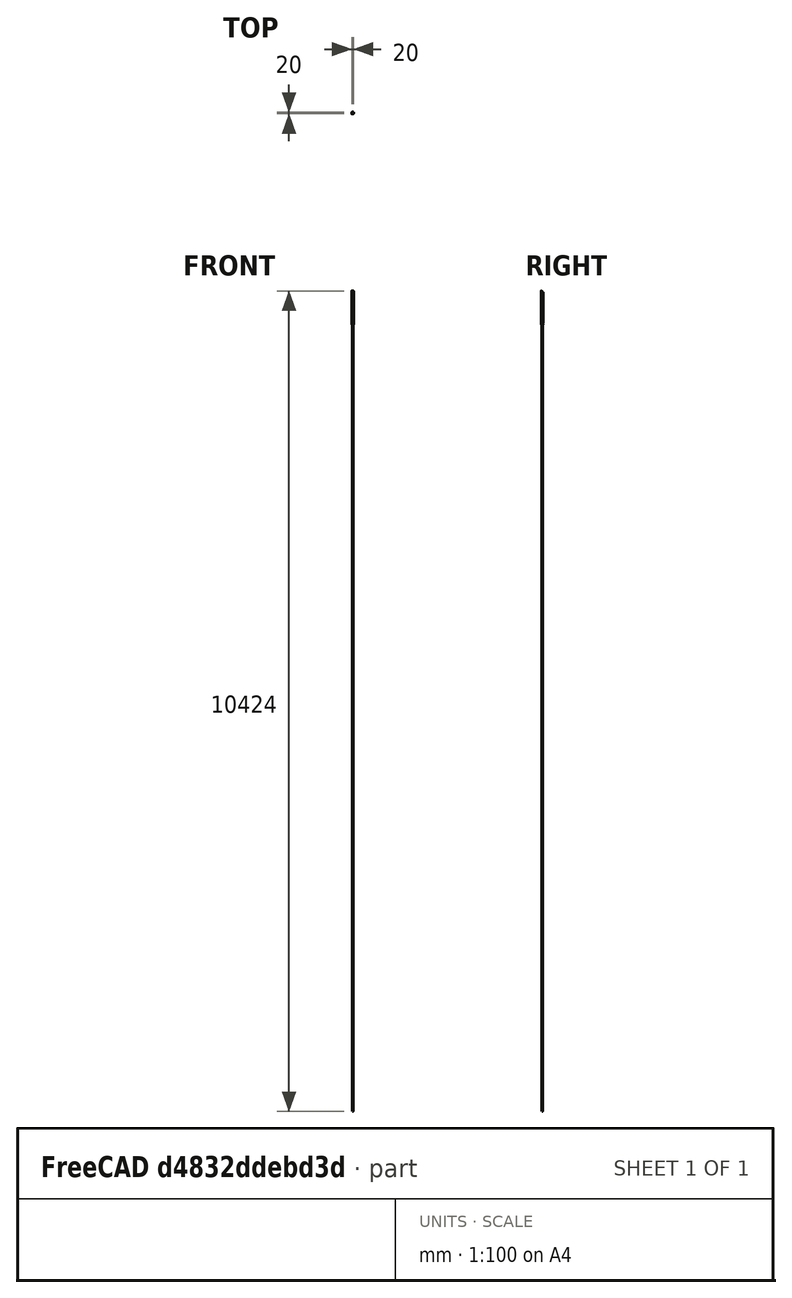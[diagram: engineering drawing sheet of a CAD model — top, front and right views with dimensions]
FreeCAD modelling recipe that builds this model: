
FCSTD DOCUMENT  (FreeCAD 0.15R4671 (Git))
Label: prueba perfil 425mm 1
License: CC-BY 3.0
LicenseURL: http://creativecommons.org/licenses/by/3.0/
objects: Sketcher::SketchObject×2, Part::Extrusion×2, Part::Cut×2, Part::Box×2, PartDesign::Pad×1, PartDesign::Pocket×1, Part::MultiFuse×1
note: 13 computed .brp shape members not serialized (recipe doc carries the construction recipe); baked Part::Feature solids carry a one-line shape summary decoded from their .brp

FEATURE [Sketcher::SketchObject] Sketch
  Placement = pos=(1.5,0,0) rot=(0,0,1;0rad)
  sketch-geometry (136):
    g0: LineSegment StartX=0 StartY=20 StartZ=0 EndX=4.65 EndY=20 EndZ=0
    g1: ArcOfCircle CenterX=-1e-12 CenterY=18.5 CenterZ=0 NormalX=0 NormalY=0 NormalZ=1 Radius=1.5 StartAngle=1.5708 EndAngle=3.14159
    g2: LineSegment StartX=-1.5 StartY=13.85 StartZ=0 EndX=-1.5 EndY=18.5 EndZ=0
    g3: ArcOfCircle CenterX=-1.3 CenterY=13.85 CenterZ=0 NormalX=0 NormalY=0 NormalZ=1 Radius=0.2 StartAngle=3.14159 EndAngle=4.71239
    g4: LineSegment StartX=-1 StartY=13.65 StartZ=0 EndX=-1.3 EndY=13.65 EndZ=0
    g5: LineSegment StartX=-1 StartY=13.3 StartZ=0 EndX=-1 EndY=13.65 EndZ=0
    g6: ArcOfCircle CenterX=-0.8 CenterY=13.3 CenterZ=0 NormalX=0 NormalY=0 NormalZ=1 Radius=0.2 StartAngle=3.14159 EndAngle=4.71239
    g7: LineSegment StartX=-0.5 StartY=13.1 StartZ=0 EndX=-0.8 EndY=13.1 EndZ=0
    g8: ArcOfCircle CenterX=-0.5 CenterY=13.6 CenterZ=0 NormalX=0 NormalY=0 NormalZ=1 Radius=0.5 StartAngle=4.71239 EndAngle=6.28319
    g9: LineSegment StartX=2.68e-07 StartY=15.5 StartZ=0 EndX=2.68e-07 EndY=13.6 EndZ=0
    g10: ArcOfCircle CenterX=0.5 CenterY=15.5 CenterZ=0 NormalX=0 NormalY=0 NormalZ=1 Radius=0.5 StartAngle=1.5708 EndAngle=3.14159
    g11: LineSegment StartX=1.23223 StartY=16 StartZ=0 EndX=0.5 EndY=16 EndZ=0
    g12: ArcOfCircle CenterX=1.23223 CenterY=15.5 CenterZ=0 NormalX=0 NormalY=0 NormalZ=1 Radius=0.5 StartAngle=0.785398 EndAngle=1.5708
    g13: LineSegment StartX=3.85355 StartY=13.5858 StartZ=0 EndX=1.58579 EndY=15.8536 EndZ=0
    g14: ArcOfCircle CenterX=3.5 CenterY=13.2322 CenterZ=0 NormalX=0 NormalY=0 NormalZ=1 Radius=0.5 StartAngle=0 EndAngle=0.785398
    g15: LineSegment StartX=4 StartY=10.9536 StartZ=0 EndX=4 EndY=13.2322 EndZ=0
    g16: ArcOfCircle CenterX=4.2 CenterY=10.9536 CenterZ=0 NormalX=0 NormalY=0 NormalZ=1 Radius=0.2 StartAngle=3.14159 EndAngle=3.66519
    g17: LineSegment StartX=4.46188 StartY=10.1 StartZ=0 EndX=4.0268 EndY=10.8536 EndZ=0
    g18: ArcOfCircle CenterX=4.28868 CenterY=10 CenterZ=0 NormalX=0 NormalY=0 NormalZ=1 Radius=0.2 StartAngle=5.75959 EndAngle=6.80678
    g19: LineSegment StartX=4.0268 StartY=9.14641 StartZ=0 EndX=4.46188 EndY=9.9 EndZ=0
    g20: ArcOfCircle CenterX=4.2 CenterY=9.04641 CenterZ=0 NormalX=0 NormalY=0 NormalZ=1 Radius=0.2 StartAngle=2.61799 EndAngle=3.14159
    g21: LineSegment StartX=4 StartY=6.76777 StartZ=0 EndX=4 EndY=9.04641 EndZ=0
    g22: ArcOfCircle CenterX=3.5 CenterY=6.76777 CenterZ=0 NormalX=0 NormalY=0 NormalZ=1 Radius=0.5 StartAngle=5.49779 EndAngle=6.28319
    g23: LineSegment StartX=1.58579 StartY=4.14645 StartZ=0 EndX=3.85355 EndY=6.41421 EndZ=0
    g24: ArcOfCircle CenterX=1.23223 CenterY=4.5 CenterZ=0 NormalX=0 NormalY=0 NormalZ=1 Radius=0.5 StartAngle=4.71239 EndAngle=5.49779
    g25: LineSegment StartX=0.5 StartY=4 StartZ=0 EndX=1.23223 EndY=4 EndZ=0
    g26: ArcOfCircle CenterX=0.5 CenterY=4.5 CenterZ=0 NormalX=0 NormalY=0 NormalZ=1 Radius=0.5 StartAngle=3.14159 EndAngle=4.71239
    g27: LineSegment StartX=2.68e-07 StartY=6.4 StartZ=0 EndX=2.68e-07 EndY=4.5 EndZ=0
    g28: ArcOfCircle CenterX=-0.5 CenterY=6.4 CenterZ=0 NormalX=0 NormalY=0 NormalZ=1 Radius=0.5 StartAngle=0 EndAngle=1.5708
    g29: LineSegment StartX=-0.8 StartY=6.9 StartZ=0 EndX=-0.5 EndY=6.9 EndZ=0
    g30: ArcOfCircle CenterX=-0.8 CenterY=6.7 CenterZ=0 NormalX=0 NormalY=0 NormalZ=1 Radius=0.2 StartAngle=1.5708 EndAngle=3.14159
    g31: LineSegment StartX=-1 StartY=6.35 StartZ=0 EndX=-1 EndY=6.7 EndZ=0
    g32: LineSegment StartX=-1.3 StartY=6.35 StartZ=0 EndX=-1 EndY=6.35 EndZ=0
    g33: ArcOfCircle CenterX=-1.3 CenterY=6.15 CenterZ=0 NormalX=0 NormalY=0 NormalZ=1 Radius=0.2 StartAngle=1.5708 EndAngle=3.14159
    g34: LineSegment StartX=-1.5 StartY=1.5 StartZ=0 EndX=-1.5 EndY=6.15 EndZ=0
    g35: ArcOfCircle CenterX=0 CenterY=1.5 CenterZ=0 NormalX=0 NormalY=0 NormalZ=1 Radius=1.5 StartAngle=3.14159 EndAngle=4.71239
    g36: LineSegment StartX=4.65 StartY=1e-12 StartZ=0 EndX=0 EndY=0 EndZ=0
    g37: ArcOfCircle CenterX=4.65 CenterY=0.2 CenterZ=0 NormalX=0 NormalY=0 NormalZ=1 Radius=0.2 StartAngle=4.71239 EndAngle=6.28319
    g38: LineSegment StartX=4.85 StartY=0.5 StartZ=0 EndX=4.85 EndY=0.2 EndZ=0
    g39: LineSegment StartX=5.2 StartY=0.5 StartZ=0 EndX=4.85 EndY=0.5 EndZ=0
    g40: ArcOfCircle CenterX=5.2 CenterY=0.7 CenterZ=0 NormalX=0 NormalY=0 NormalZ=1 Radius=0.2 StartAngle=4.71239 EndAngle=6.28319
    g41: LineSegment StartX=5.4 StartY=1 StartZ=0 EndX=5.4 EndY=0.7 EndZ=0
    g42: ArcOfCircle CenterX=4.9 CenterY=1 CenterZ=0 NormalX=0 NormalY=0 NormalZ=1 Radius=0.5 StartAngle=0 EndAngle=1.5708
    g43: LineSegment StartX=3 StartY=1.5 StartZ=0 EndX=4.9 EndY=1.5 EndZ=0
    g44: ArcOfCircle CenterX=3 CenterY=2 CenterZ=0 NormalX=0 NormalY=0 NormalZ=1 Radius=0.5 StartAngle=3.14159 EndAngle=4.71239
    g45: LineSegment StartX=2.5 StartY=2.73223 StartZ=0 EndX=2.5 EndY=2 EndZ=0
    g46: ArcOfCircle CenterX=3 CenterY=2.73223 CenterZ=0 NormalX=0 NormalY=0 NormalZ=1 Radius=0.5 StartAngle=2.35619 EndAngle=3.14159
    g47: LineSegment StartX=4.91421 StartY=5.35355 StartZ=0 EndX=2.64645 EndY=3.08579 EndZ=0
    g48: ArcOfCircle CenterX=5.26777 CenterY=5 CenterZ=0 NormalX=0 NormalY=0 NormalZ=1 Radius=0.5 StartAngle=1.5708 EndAngle=2.35619
    g49: LineSegment StartX=7.54641 StartY=5.5 StartZ=0 EndX=5.26777 EndY=5.5 EndZ=0
    g50: ArcOfCircle CenterX=7.54641 CenterY=5.7 CenterZ=0 NormalX=0 NormalY=0 NormalZ=1 Radius=0.2 StartAngle=4.71239 EndAngle=5.23599
    g51: LineSegment StartX=8.4 StartY=5.96188 StartZ=0 EndX=7.64641 EndY=5.52679 EndZ=0
    g52: ArcOfCircle CenterX=8.5 CenterY=5.78868 CenterZ=0 NormalX=0 NormalY=0 NormalZ=1 Radius=0.2 StartAngle=1.0472 EndAngle=2.0944
    g53: LineSegment StartX=9.35359 StartY=5.52679 StartZ=0 EndX=8.6 EndY=5.96188 EndZ=0
    g54: ArcOfCircle CenterX=9.45359 CenterY=5.7 CenterZ=0 NormalX=0 NormalY=0 NormalZ=1 Radius=0.2 StartAngle=4.18879 EndAngle=4.71239
    g55: LineSegment StartX=11.7322 StartY=5.5 StartZ=0 EndX=9.45359 EndY=5.5 EndZ=0
    g56: ArcOfCircle CenterX=11.7322 CenterY=5 CenterZ=0 NormalX=0 NormalY=0 NormalZ=1 Radius=0.5 StartAngle=0.785398 EndAngle=1.5708
    g57: LineSegment StartX=14.3536 StartY=3.08579 StartZ=0 EndX=12.0858 EndY=5.35355 EndZ=0
    g58: ArcOfCircle CenterX=14 CenterY=2.73223 CenterZ=0 NormalX=0 NormalY=0 NormalZ=1 Radius=0.5 StartAngle=0 EndAngle=0.785398
    g59: LineSegment StartX=14.5 StartY=2 StartZ=0 EndX=14.5 EndY=2.73223 EndZ=0
    g60: ArcOfCircle CenterX=14 CenterY=2 CenterZ=0 NormalX=0 NormalY=0 NormalZ=1 Radius=0.5 StartAngle=4.71239 EndAngle=6.28319
    g61: LineSegment StartX=12.1 StartY=1.5 StartZ=0 EndX=14 EndY=1.5 EndZ=0
    g62: ArcOfCircle CenterX=12.1 CenterY=1 CenterZ=0 NormalX=0 NormalY=0 NormalZ=1 Radius=0.5 StartAngle=1.5708 EndAngle=3.14159
    g63: LineSegment StartX=11.6 StartY=0.7 StartZ=0 EndX=11.6 EndY=1 EndZ=0
    g64: ArcOfCircle CenterX=11.8 CenterY=0.7 CenterZ=0 NormalX=0 NormalY=0 NormalZ=1 Radius=0.2 StartAngle=3.14159 EndAngle=4.71239
    g65: LineSegment StartX=12.15 StartY=0.5 StartZ=0 EndX=11.8 EndY=0.5 EndZ=0
    g66: LineSegment StartX=12.15 StartY=0.2 StartZ=0 EndX=12.15 EndY=0.5 EndZ=0
    g67: ArcOfCircle CenterX=12.35 CenterY=0.2 CenterZ=0 NormalX=0 NormalY=0 NormalZ=1 Radius=0.2 StartAngle=3.14159 EndAngle=4.71239
    g68: LineSegment StartX=17 StartY=1e-12 StartZ=0 EndX=12.35 EndY=0 EndZ=0
    g69: ArcOfCircle CenterX=17 CenterY=1.5 CenterZ=0 NormalX=0 NormalY=0 NormalZ=1 Radius=1.5 StartAngle=4.71239 EndAngle=6.28319
    g70: LineSegment StartX=18.5 StartY=6.15 StartZ=0 EndX=18.5 EndY=1.5 EndZ=0
    g71: ArcOfCircle CenterX=18.3 CenterY=6.15 CenterZ=0 NormalX=0 NormalY=0 NormalZ=1 Radius=0.2 StartAngle=0 EndAngle=1.5708
    g72: LineSegment StartX=18 StartY=6.35 StartZ=0 EndX=18.3 EndY=6.35 EndZ=0
    g73: LineSegment StartX=18 StartY=6.7 StartZ=0 EndX=18 EndY=6.35 EndZ=0
    g74: ArcOfCircle CenterX=17.8 CenterY=6.7 CenterZ=0 NormalX=0 NormalY=0 NormalZ=1 Radius=0.2 StartAngle=0 EndAngle=1.5708
    g75: LineSegment StartX=17.5 StartY=6.9 StartZ=0 EndX=17.8 EndY=6.9 EndZ=0
    g76: ArcOfCircle CenterX=17.5 CenterY=6.4 CenterZ=0 NormalX=0 NormalY=0 NormalZ=1 Radius=0.5 StartAngle=1.5708 EndAngle=3.14159
    g77: LineSegment StartX=17 StartY=4.5 StartZ=0 EndX=17 EndY=6.4 EndZ=0
    g78: ArcOfCircle CenterX=16.5 CenterY=4.5 CenterZ=0 NormalX=0 NormalY=0 NormalZ=1 Radius=0.5 StartAngle=4.71239 EndAngle=6.28319
    g79: LineSegment StartX=15.7678 StartY=4 StartZ=0 EndX=16.5 EndY=4 EndZ=0
    g80: ArcOfCircle CenterX=15.7678 CenterY=4.5 CenterZ=0 NormalX=0 NormalY=0 NormalZ=1 Radius=0.5 StartAngle=3.92699 EndAngle=4.71239
    g81: LineSegment StartX=13.1464 StartY=6.41421 StartZ=0 EndX=15.4142 EndY=4.14645 EndZ=0
    g82: ArcOfCircle CenterX=13.5 CenterY=6.76777 CenterZ=0 NormalX=0 NormalY=0 NormalZ=1 Radius=0.5 StartAngle=3.14159 EndAngle=3.92699
    g83: LineSegment StartX=13 StartY=9.04641 StartZ=0 EndX=13 EndY=6.76777 EndZ=0
    g84: ArcOfCircle CenterX=12.8 CenterY=9.04641 CenterZ=0 NormalX=0 NormalY=0 NormalZ=1 Radius=0.2 StartAngle=0 EndAngle=0.523599
    g85: LineSegment StartX=12.5381 StartY=9.9 StartZ=0 EndX=12.9732 EndY=9.14641 EndZ=0
    g86: ArcOfCircle CenterX=12.7113 CenterY=10 CenterZ=0 NormalX=0 NormalY=0 NormalZ=1 Radius=0.2 StartAngle=2.61799 EndAngle=3.66519
    g87: LineSegment StartX=12.9732 StartY=10.8536 StartZ=0 EndX=12.5381 EndY=10.1 EndZ=0
    g88: ArcOfCircle CenterX=12.8 CenterY=10.9536 CenterZ=0 NormalX=0 NormalY=0 NormalZ=1 Radius=0.2 StartAngle=5.75959 EndAngle=6.28319
    g89: LineSegment StartX=13 StartY=13.2322 StartZ=0 EndX=13 EndY=10.9536 EndZ=0
    g90: ArcOfCircle CenterX=13.5 CenterY=13.2322 CenterZ=0 NormalX=0 NormalY=0 NormalZ=1 Radius=0.5 StartAngle=2.35619 EndAngle=3.14159
    g91: LineSegment StartX=15.4142 StartY=15.8536 StartZ=0 EndX=13.1464 EndY=13.5858 EndZ=0
    g92: ArcOfCircle CenterX=15.7678 CenterY=15.5 CenterZ=0 NormalX=0 NormalY=0 NormalZ=1 Radius=0.5 StartAngle=1.5708 EndAngle=2.35619
    g93: LineSegment StartX=16.5 StartY=16 StartZ=0 EndX=15.7678 EndY=16 EndZ=0
    g94: ArcOfCircle CenterX=16.5 CenterY=15.5 CenterZ=0 NormalX=0 NormalY=0 NormalZ=1 Radius=0.5 StartAngle=0 EndAngle=1.5708
    g95: LineSegment StartX=17 StartY=13.6 StartZ=0 EndX=17 EndY=15.5 EndZ=0
    g96: ArcOfCircle CenterX=17.5 CenterY=13.6 CenterZ=0 NormalX=0 NormalY=0 NormalZ=1 Radius=0.5 StartAngle=3.14159 EndAngle=4.71239
    g97: LineSegment StartX=17.8 StartY=13.1 StartZ=0 EndX=17.5 EndY=13.1 EndZ=0
    g98: ArcOfCircle CenterX=17.8 CenterY=13.3 CenterZ=0 NormalX=0 NormalY=0 NormalZ=1 Radius=0.2 StartAngle=4.71239 EndAngle=6.28319
    g99: LineSegment StartX=18 StartY=13.65 StartZ=0 EndX=18 EndY=13.3 EndZ=0
    g100: LineSegment StartX=18.3 StartY=13.65 StartZ=0 EndX=18 EndY=13.65 EndZ=0
    g101: ArcOfCircle CenterX=18.3 CenterY=13.85 CenterZ=0 NormalX=0 NormalY=0 NormalZ=1 Radius=0.2 StartAngle=4.71239 EndAngle=6.28319
    g102: LineSegment StartX=18.5 StartY=18.5 StartZ=0 EndX=18.5 EndY=13.85 EndZ=0
    g103: ArcOfCircle CenterX=17 CenterY=18.5 CenterZ=0 NormalX=0 NormalY=0 NormalZ=1 Radius=1.5 StartAngle=0 EndAngle=1.5708
    g104: LineSegment StartX=12.35 StartY=20 StartZ=0 EndX=17 EndY=20 EndZ=0
    g105: ArcOfCircle CenterX=12.35 CenterY=19.8 CenterZ=0 NormalX=0 NormalY=0 NormalZ=1 Radius=0.2 StartAngle=1.5708 EndAngle=3.14159
    g106: LineSegment StartX=12.15 StartY=19.5 StartZ=0 EndX=12.15 EndY=19.8 EndZ=0
    g107: LineSegment StartX=11.8 StartY=19.5 StartZ=0 EndX=12.15 EndY=19.5 EndZ=0
    g108: ArcOfCircle CenterX=11.8 CenterY=19.3 CenterZ=0 NormalX=0 NormalY=0 NormalZ=1 Radius=0.2 StartAngle=1.5708 EndAngle=3.14159
    g109: LineSegment StartX=11.6 StartY=19 StartZ=0 EndX=11.6 EndY=19.3 EndZ=0
    g110: ArcOfCircle CenterX=12.1 CenterY=19 CenterZ=0 NormalX=0 NormalY=0 NormalZ=1 Radius=0.5 StartAngle=3.14159 EndAngle=4.71239
    g111: LineSegment StartX=14 StartY=18.5 StartZ=0 EndX=12.1 EndY=18.5 EndZ=0
    g112: ArcOfCircle CenterX=14 CenterY=18 CenterZ=0 NormalX=0 NormalY=0 NormalZ=1 Radius=0.5 StartAngle=0 EndAngle=1.5708
    g113: LineSegment StartX=14.5 StartY=17.2678 StartZ=0 EndX=14.5 EndY=18 EndZ=0
    g114: ArcOfCircle CenterX=14 CenterY=17.2678 CenterZ=0 NormalX=0 NormalY=0 NormalZ=1 Radius=0.5 StartAngle=5.49779 EndAngle=6.28319
    g115: LineSegment StartX=12.0858 StartY=14.6464 StartZ=0 EndX=14.3536 EndY=16.9142 EndZ=0
    g116: ArcOfCircle CenterX=11.7322 CenterY=15 CenterZ=0 NormalX=0 NormalY=0 NormalZ=1 Radius=0.5 StartAngle=4.71239 EndAngle=5.49779
    g117: LineSegment StartX=9.45359 StartY=14.5 StartZ=0 EndX=11.7322 EndY=14.5 EndZ=0
    g118: ArcOfCircle CenterX=9.45359 CenterY=14.3 CenterZ=0 NormalX=0 NormalY=0 NormalZ=1 Radius=0.2 StartAngle=1.5708 EndAngle=2.0944
    g119: LineSegment StartX=8.6 StartY=14.0381 StartZ=0 EndX=9.35359 EndY=14.4732 EndZ=0
    g120: ArcOfCircle CenterX=8.5 CenterY=14.2113 CenterZ=0 NormalX=0 NormalY=0 NormalZ=1 Radius=0.2 StartAngle=4.18879 EndAngle=5.23599
    g121: LineSegment StartX=7.64641 StartY=14.4732 StartZ=0 EndX=8.4 EndY=14.0381 EndZ=0
    g122: ArcOfCircle CenterX=7.54641 CenterY=14.3 CenterZ=0 NormalX=0 NormalY=0 NormalZ=1 Radius=0.2 StartAngle=1.0472 EndAngle=1.5708
    g123: LineSegment StartX=5.26777 StartY=14.5 StartZ=0 EndX=7.54641 EndY=14.5 EndZ=0
    g124: ArcOfCircle CenterX=5.26777 CenterY=15 CenterZ=0 NormalX=0 NormalY=0 NormalZ=1 Radius=0.5 StartAngle=3.92699 EndAngle=4.71239
    g125: LineSegment StartX=2.64645 StartY=16.9142 StartZ=0 EndX=4.91421 EndY=14.6464 EndZ=0
    g126: ArcOfCircle CenterX=3 CenterY=17.2678 CenterZ=0 NormalX=0 NormalY=0 NormalZ=1 Radius=0.5 StartAngle=3.14159 EndAngle=3.92699
    g127: LineSegment StartX=2.5 StartY=18 StartZ=0 EndX=2.5 EndY=17.2678 EndZ=0
    g128: ArcOfCircle CenterX=3 CenterY=18 CenterZ=0 NormalX=0 NormalY=0 NormalZ=1 Radius=0.5 StartAngle=1.5708 EndAngle=3.14159
    g129: LineSegment StartX=4.9 StartY=18.5 StartZ=0 EndX=3 EndY=18.5 EndZ=0
    g130: ArcOfCircle CenterX=4.9 CenterY=19 CenterZ=0 NormalX=0 NormalY=0 NormalZ=1 Radius=0.5 StartAngle=4.71239 EndAngle=6.28319
    g131: LineSegment StartX=5.4 StartY=19.3 StartZ=0 EndX=5.4 EndY=19 EndZ=0
    g132: ArcOfCircle CenterX=5.2 CenterY=19.3 CenterZ=0 NormalX=0 NormalY=0 NormalZ=1 Radius=0.2 StartAngle=0 EndAngle=1.5708
    g133: LineSegment StartX=4.85 StartY=19.5 StartZ=0 EndX=5.2 EndY=19.5 EndZ=0
    g134: LineSegment StartX=4.85 StartY=19.8 StartZ=0 EndX=4.85 EndY=19.5 EndZ=0
    g135: ArcOfCircle CenterX=4.65 CenterY=19.8 CenterZ=0 NormalX=0 NormalY=0 NormalZ=1 Radius=0.2 StartAngle=0 EndAngle=1.5708
  constraints (136):
    c: Coincident(g0,g1)
    c: Coincident(g135,g0)
    c: Coincident(g1,g2)
    c: Coincident(g2,g3)
    c: Coincident(g3,g4)
    c: Coincident(g4,g5)
    c: Coincident(g6,g5)
    c: Coincident(g7,g6)
    c: Coincident(g8,g7)
    c: Coincident(g9,g8)
    c: Coincident(g10,g9)
    c: Coincident(g10,g11)
    c: Coincident(g11,g12)
    c: Coincident(g12,g13)
    c: Coincident(g14,g13)
    c: Coincident(g15,g14)
    c: Coincident(g15,g16)
    c: Coincident(g16,g17)
    c: Coincident(g17,g18)
    c: Coincident(g18,g19)
    c: Coincident(g19,g20)
    c: Coincident(g20,g21)
    c: Coincident(g21,g22)
    c: Coincident(g22,g23)
    c: Coincident(g23,g24)
    c: Coincident(g24,g25)
    c: Coincident(g26,g25)
    c: Coincident(g26,g27)
    c: Coincident(g28,g27)
    c: Coincident(g28,g29)
    c: Coincident(g30,g29)
    c: Coincident(g31,g30)
    c: Coincident(g31,g32)
    c: Coincident(g32,g33)
    c: Coincident(g33,g34)
    c: Coincident(g35,g34)
    c: Coincident(g36,g35)
    c: Coincident(g37,g36)
    c: Coincident(g37,g38)
    c: Coincident(g38,g39)
    c: Coincident(g40,g39)
    c: Coincident(g40,g41)
    c: Coincident(g41,g42)
    c: Coincident(g43,g42)
    c: Coincident(g44,g43)
    c: Coincident(g44,g45)
    c: Coincident(g45,g46)
    c: Coincident(g46,g47)
    c: Coincident(g47,g48)
    c: Coincident(g49,g48)
    c: Coincident(g49,g50)
    c: Coincident(g50,g51)
    c: Coincident(g51,g52)
    c: Coincident(g53,g52)
    c: Coincident(g54,g53)
    c: Coincident(g55,g54)
    c: Coincident(g56,g55)
    c: Coincident(g56,g57)
    c: Coincident(g58,g57)
    c: Coincident(g59,g58)
    c: Coincident(g60,g59)
    c: Coincident(g61,g60)
    c: Coincident(g62,g61)
    c: Coincident(g62,g63)
    c: Coincident(g64,g63)
    c: Coincident(g65,g64)
    c: Coincident(g66,g65)
    c: Coincident(g67,g66)
    c: Coincident(g67,g68)
    c: Coincident(g69,g68)
    c: Coincident(g70,g69)
    c: Coincident(g71,g70)
    c: Coincident(g72,g71)
    c: Coincident(g73,g72)
    c: Coincident(g73,g74)
    c: Coincident(g75,g74)
    c: Coincident(g76,g75)
    c: Coincident(g76,g77)
    c: Coincident(g77,g78)
    c: Coincident(g78,g79)
    c: Coincident(g80,g79)
    c: Coincident(g81,g80)
    c: Coincident(g81,g82)
    c: Coincident(g82,g83)
    c: Coincident(g83,g84)
    c: Coincident(g85,g84)
    c: Coincident(g86,g85)
    c: Coincident(g86,g87)
    c: Coincident(g88,g87)
    c: Coincident(g88,g89)
    c: Coincident(g89,g90)
    c: Coincident(g91,g90)
    c: Coincident(g92,g91)
    c: Coincident(g93,g92)
    c: Coincident(g94,g93)
    c: Coincident(g94,g95)
    c: Coincident(g95,g96)
    c: Coincident(g96,g97)
    c: Coincident(g98,g97)
    c: Coincident(g98,g99)
    c: Coincident(g100,g99)
    c: Coincident(g100,g101)
    c: Coincident(g101,g102)
    c: Coincident(g102,g103)
    c: Coincident(g103,g104)
    c: Coincident(g104,g105)
    c: Coincident(g106,g105)
    c: Coincident(g107,g106)
    c: Coincident(g108,g107)
    c: Coincident(g109,g108)
    c: Coincident(g110,g109)
    c: Coincident(g111,g110)
    c: Coincident(g112,g111)
    c: Coincident(g112,g113)
    c: Coincident(g113,g114)
    c: Coincident(g114,g115)
    c: Coincident(g115,g116)
    c: Coincident(g117,g116)
    c: Coincident(g118,g117)
    c: Coincident(g119,g118)
    c: Coincident(g119,g120)
    c: Coincident(g121,g120)
    c: Coincident(g121,g122)
    c: Coincident(g122,g123)
    c: Coincident(g124,g123)
    c: Coincident(g124,g125)
    c: Coincident(g126,g125)
    c: Coincident(g127,g126)
    c: Coincident(g128,g127)
    c: Coincident(g129,g128)
    c: Coincident(g130,g129)
    c: Coincident(g130,g131)
    c: Coincident(g131,g132)
    c: Coincident(g133,g132)
    c: Coincident(g134,g133)
    c: Coincident(g135,g134)
FEATURE [PartDesign::Pad] Pad
  Length = 5
  Length2 = 100
  Placement = pos=(1.5,0,0) rot=(0,0,1;0rad)
  Sketch = -> Sketch
  Type = 0
FEATURE [Sketcher::SketchObject] Sketch001
  Placement = pos=(1.5,0,5) rot=(0,0,1;0rad)
  Support = -> Pad [Face138]
  sketch-geometry (16):
    g0: ArcOfCircle CenterX=8.5 CenterY=10 CenterZ=0 NormalX=0 NormalY=0 NormalZ=1 Radius=3.54978 StartAngle=2.14023 EndAngle=2.57348
    g1: LineSegment StartX=6.5861 StartY=12.9896 StartZ=0 EndX=7.24181 EndY=12.4453 EndZ=0
    g2: ArcOfCircle CenterX=8.5 CenterY=10 CenterZ=0 NormalX=0 NormalY=0 NormalZ=1 Radius=2.75 StartAngle=1.09559 EndAngle=2.046
    g3: LineSegment StartX=9.75819 StartY=12.4453 StartZ=0 EndX=10.4139 EndY=12.9896 EndZ=0
    g4: ArcOfCircle CenterX=8.5 CenterY=10 CenterZ=0 NormalX=0 NormalY=0 NormalZ=1 Radius=3.54978 StartAngle=0.568112 EndAngle=1.00136
    g5: LineSegment StartX=11.4922 StartY=11.9099 StartZ=0 EndX=10.9453 EndY=11.2582 EndZ=0
    g6: ArcOfCircle CenterX=8.5 CenterY=10 CenterZ=0 NormalX=0 NormalY=0 NormalZ=1 Radius=2.75 StartAngle=5.80798 EndAngle=6.75839
    g7: LineSegment StartX=10.9453 StartY=8.74181 StartZ=0 EndX=11.4922 EndY=8.09007 EndZ=0
    g8: ArcOfCircle CenterX=8.5 CenterY=10 CenterZ=0 NormalX=0 NormalY=0 NormalZ=1 Radius=3.54978 StartAngle=5.28183 EndAngle=5.71507
    g9: LineSegment StartX=10.4139 StartY=7.01036 StartZ=0 EndX=9.75819 EndY=7.5547 EndZ=0
    g10: ArcOfCircle CenterX=8.5 CenterY=10 CenterZ=0 NormalX=0 NormalY=0 NormalZ=1 Radius=2.75 StartAngle=4.23718 EndAngle=5.1876
    g11: LineSegment StartX=7.24181 StartY=7.5547 StartZ=0 EndX=6.5861 EndY=7.01036 EndZ=0
    g12: ArcOfCircle CenterX=8.5 CenterY=10 CenterZ=0 NormalX=0 NormalY=0 NormalZ=1 Radius=3.54978 StartAngle=3.7097 EndAngle=4.14295
    g13: LineSegment StartX=5.50783 StartY=8.09007 StartZ=0 EndX=6.0547 EndY=8.74181 EndZ=0
    g14: ArcOfCircle CenterX=8.5 CenterY=10 CenterZ=0 NormalX=0 NormalY=0 NormalZ=1 Radius=2.75 StartAngle=2.66639 EndAngle=3.6168
    g15: LineSegment StartX=6.0547 StartY=11.2582 StartZ=0 EndX=5.50783 EndY=11.9099 EndZ=0
  constraints (16):
    c: Coincident(g0,g1)
    c: Coincident(g15,g0)
    c: Coincident(g1,g2)
    c: Coincident(g3,g2)
    c: Coincident(g4,g3)
    c: Coincident(g4,g5)
    c: Coincident(g6,g5)
    c: Coincident(g7,g6)
    c: Coincident(g8,g7)
    c: Coincident(g9,g8)
    c: Coincident(g10,g9)
    c: Coincident(g11,g10)
    c: Coincident(g12,g11)
    c: Coincident(g13,g12)
    c: Coincident(g14,g13)
    c: Coincident(g15,g14)
FEATURE [PartDesign::Pocket] Pocket
  Length = 5
  Placement = pos=(1.5,0,0) rot=(0,0,1;0rad)
  Sketch = -> Sketch001
  Type = 1
FEATURE [Part::Extrusion] Extrude
  Base = -> Sketch
  Dir = (0,0,427)
  Placement = pos=(0,0,2) rot=(0,0,1;0rad)
  Solid = true
FEATURE [Part::Extrusion] Extrude001
  Base = -> Sketch001
  Dir = (0,0,431)
  Placement = pos=(0,0,-4) rot=(0,0,1;0rad)
  Solid = true
FEATURE [Part::Cut] Cut  label="perfil 425"
  Base = -> Extrude
  Tool = -> Extrude001
FEATURE [Part::Box] Box  label="Cubo"
  Height = 26
  Length = 30
  Placement = pos=(-5,5,-29) rot=(1,0,0;0.785398rad)
  Width = 57
FEATURE [Part::Box] Box001  label="Cubo001"
  Height = 25
  Length = 30
  Placement = pos=(-5,-1,430) rot=(-1,0,0;0.785398rad)
  Width = 35
FEATURE [Part::MultiFuse] Fusion
  Shapes = -> [Box,Box001]
FEATURE [Part::Cut] Cut001
  Base = -> Cut
  Tool = -> Fusion
